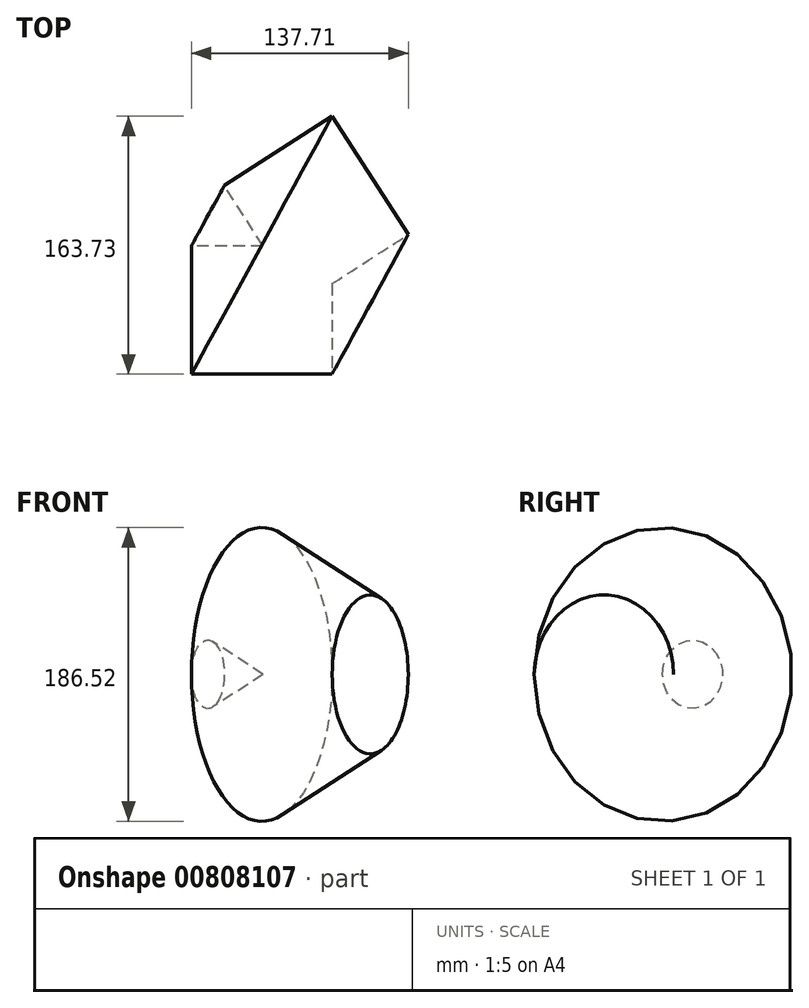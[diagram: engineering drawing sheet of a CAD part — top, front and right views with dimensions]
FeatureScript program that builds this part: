
annotation { "Feature Type Name" : "Feature", "Feature Type Description" : "" }
export const myFeature = defineFeature(function(context is Context, id is Id, definition is map)
    precondition{}
    {
        {
            var Q0;
            Q0=qCreatedBy(makeId("Top.planeOp"),FACE);
            var sketch = newSketch(context, id + "F0", { "sketchPlane" : qUnion([Q0])});
            skLineSegment(sketch, "E0.bottom", {"start": v(-44.12, 38.16) * mm, "end": v(45.25, 38.16) * mm});
            skLineSegment(sketch, "E0.top", {"start": v(-44.12, -43.27) * mm, "end": v(45.25, -43.27) * mm});
            skLineSegment(sketch, "E0.left", {"start": v(-44.12, 38.16) * mm, "end": v(-44.12, -43.27) * mm});
            skLineSegment(sketch, "E0.right", {"start": v(45.25, 38.16) * mm, "end": v(45.25, -43.27) * mm});
            skLineSegment(sketch, "E1", {"start": v(-22.56, 51.21) * mm, "end": v(61.14, 5.53) * mm});
            skSolve(sketch);
        }
        {
            var Q0;
            {var subQ1=sQuery(id+"F0.wireOp",EDGE,"E0.top");Q0=makeQuery(id+"F0.imprint","IMPRINT",FACE,{"disambiguationData":[TD([[makeQuery(id+"F0.imprint","IMPRINT",EDGE,{"derivedFrom":subQ1}),1.0]])]});}
            var Q1;
            Q1=sQuery(id+"F0.wireOp",EDGE,"E1");
            revolve(context, id + "F1", {"surfaceOperationType" : NewSurfaceOperationType.NEW, "entities" : qUnion([Q0]), "axis" : qUnion([Q1]), "revolveType" : RevolveType.FULL});
        }
    });
